FCSTD DOCUMENT  (FreeCAD 0.19R0.19.2)
Label: laptopStand003
License: All rights reserved
LicenseURL: http://en.wikipedia.org/wiki/All_rights_reserved
objects: Sketcher::SketchObject×1
note: 1 computed .brp shape members not serialized (recipe doc carries the construction recipe); baked Part::Feature solids carry a one-line shape summary decoded from their .brp

FEATURE [Sketcher::SketchObject] Sketch
  FullyConstrained = false
  sketch-geometry (10):
    g0: LineSegment StartX=-22.9272 StartY=136.221 StartZ=0 EndX=-22.9272 EndY=-103.779 EndZ=0
    g1: LineSegment StartX=-22.9272 StartY=136.221 StartZ=0 EndX=387.073 EndY=136.221 EndZ=0
    g2: LineSegment StartX=66.1121 StartY=95.2117 StartZ=0 EndX=66.1121 EndY=-84.7883 EndZ=0
    g3: LineSegment StartX=66.1121 StartY=95.2117 StartZ=0 EndX=256.112 EndY=95.2117 EndZ=0
    g4: LineSegment StartX=256.112 StartY=95.2117 StartZ=0 EndX=271.112 EndY=95.2117 EndZ=0
    g5: LineSegment StartX=256.112 StartY=83.2117 StartZ=0 EndX=78.1121 EndY=83.2117 EndZ=0
    g6: LineSegment StartX=78.1121 StartY=-84.7883 StartZ=0 EndX=78.1121 EndY=83.2117 EndZ=0
    g7: LineSegment StartX=271.112 StartY=83.2117 StartZ=0 EndX=286.112 EndY=83.2117 EndZ=0
    g8: LineSegment StartX=286.112 StartY=83.2117 StartZ=0 EndX=464.112 EndY=83.2117 EndZ=0
    g9: LineSegment StartX=286.112 StartY=95.2117 StartZ=0 EndX=476.112 EndY=95.2117 EndZ=0
  constraints (28):
    c: Vertical(g0)
    c: Distance(g0) = 240
    c: Horizontal(g1)
    c: Distance(g1) = 410
    c: Coincident(g1,g0)
    c: Vertical(g2)
    c: Distance(g2) = 180
    c: Horizontal(g3)
    c: Distance(g3) = 190
    c: Coincident(g3,g2)
    c: Horizontal(g4)
    c: Distance(g4) = 15
    c: Coincident(g4,g3)
    c: Block(g2)
    c: Horizontal(g5)
    c: Vertical(g6)
    c: Coincident(g5,g6)
    c: Block(g5)
    c: Block(g6)
    c: Horizontal(g7)
    c: Distance(g7) = 15
    c: Block(g7)
    c: Coincident(g8,g7)
    c: Horizontal(g8)
    c: Horizontal(g9)
    c: Distance(g9) = 190
    c: Distance(g8) = 178
    c: Block(g9)
